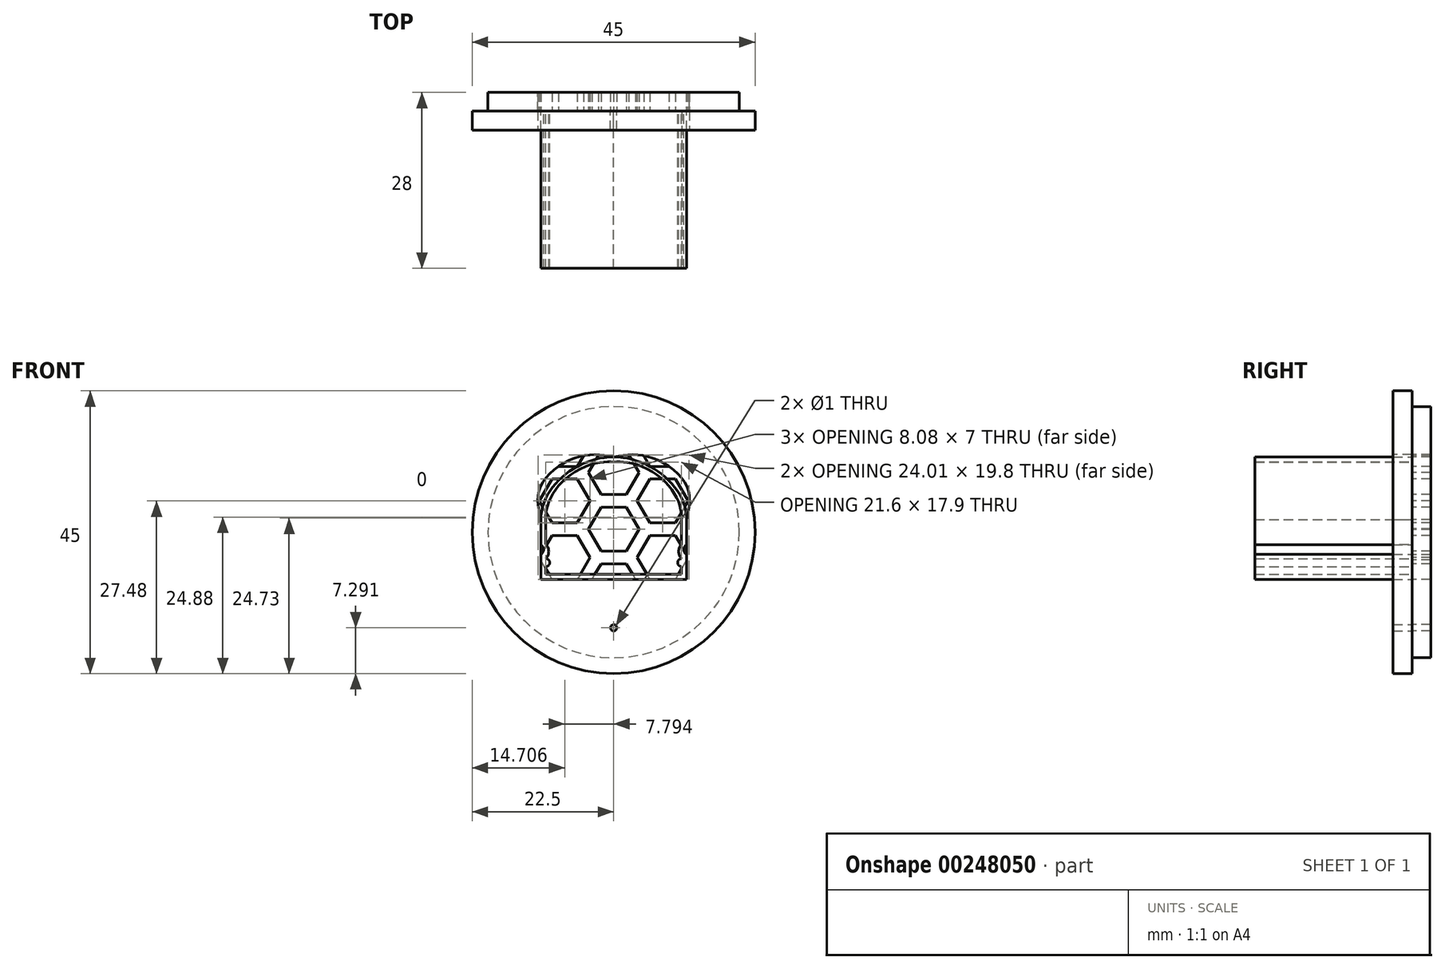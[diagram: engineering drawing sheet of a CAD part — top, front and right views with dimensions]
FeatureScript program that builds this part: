
annotation { "Feature Type Name" : "Feature", "Feature Type Description" : "" }
export const myFeature = defineFeature(function(context is Context, id is Id, definition is map)
    precondition{}
    {
        {
            var Q0;
            Q0=qCreatedBy(makeId("Front.planeOp"),FACE);
            var sketch = newSketch(context, id + "F0", { "sketchPlane" : qUnion([Q0])});
            skLineSegment(sketch, "E0", {"start": v(-11.6, 0) * mm, "end": v(11.6, 0) * mm});
            skLineSegment(sketch, "E1", {"start": v(11.6, 0) * mm, "end": v(11.6, 4) * mm});
            skLineSegment(sketch, "E2", {"start": v(11.6, 5.5) * mm, "end": v(11.6, 9.5) * mm});
            skLineSegment(sketch, "E3", {"start": v(0, 0) * mm, "end": v(0, 19.5) * mm, "construction": true});
            skFitSpline(sketch, "E4", {"points": [v(11.6, 9.5) * mm, v(0, 19.5) * mm], "startDerivative": vector(0, 16.22) * mm, "endDerivative": vector(-17.13, 0) * mm});
            skLineSegment(sketch, "E5", {"start": v(0, 0.8) * mm, "end": v(10.8, 0.8) * mm});
            skLineSegment(sketch, "E6", {"start": v(10.8, 0.8) * mm, "end": v(10.8, 2.05) * mm});
            skArc(sketch, "E7", {"start": v(10.8, 3.3) * mm, "mid": v(10.17, 2.67) * mm, "end": v(10.8, 2.05) * mm});
            skArc(sketch, "E8", {"start": v(10.8, 5.6) * mm, "mid": v(10.34, 4.45) * mm, "end": v(10.8, 3.3) * mm});
            skArc(sketch, "E9", {"start": v(11.6, 5.5) * mm, "mid": v(11.15, 4.75) * mm, "end": v(11.6, 4) * mm});
            skLineSegment(sketch, "E10.1", {"start": v(10.8, 5.6) * mm, "end": v(10.8, 9.5) * mm});
            skLineSegment(sketch, "E11.MirrorCS", {"start": v(-10.8, 0.8) * mm, "end": v(-10.8, 2.05) * mm});
            skArc(sketch, "E12.MirrorCS", {"start": v(-11.6, 5.5) * mm, "mid": v(-11.15, 4.75) * mm, "end": v(-11.6, 4) * mm});
            skLineSegment(sketch, "E13.MirrorCS", {"start": v(-11.6, 0) * mm, "end": v(-11.6, 4) * mm});
            skLineSegment(sketch, "E14.MirrorCS", {"start": v(-11.6, 5.5) * mm, "end": v(-11.6, 9.5) * mm});
            skFitSpline(sketch, "E15.MirrorCS", {"points": [v(-11.6, 9.5) * mm, v(0, 19.5) * mm], "startDerivative": vector(0, 16.22) * mm, "endDerivative": vector(17.13, 0) * mm});
            skLineSegment(sketch, "E16.MirrorCS", {"start": v(0, 0.8) * mm, "end": v(-10.8, 0.8) * mm});
            skArc(sketch, "E17.MirrorCS", {"start": v(-10.8, 5.6) * mm, "mid": v(-10.34, 4.45) * mm, "end": v(-10.8, 3.3) * mm});
            skArc(sketch, "E18.MirrorCS", {"start": v(-10.8, 3.3) * mm, "mid": v(-10.17, 2.67) * mm, "end": v(-10.8, 2.05) * mm});
            skLineSegment(sketch, "E19.MirrorCS", {"start": v(-10.8, 5.6) * mm, "end": v(-10.8, 9.5) * mm});
            skFitSpline(sketch, "E20.0", {"points": [v(-10.8, 9.5) * mm, v(-10.8, 10.1) * mm, v(-10.64, 11.29) * mm, v(-9.72, 13.55) * mm, v(-7.6, 16.07) * mm, v(-4.01, 18.17) * mm, v(-1.32, 18.7) * mm, v(0, 18.7) * mm]});
            skFitSpline(sketch, "E20.1", {"points": [v(10.8, 9.5) * mm, v(10.8, 10.1) * mm, v(10.64, 11.29) * mm, v(9.72, 13.55) * mm, v(7.6, 16.07) * mm, v(4.01, 18.17) * mm, v(1.32, 18.7) * mm, v(0, 18.7) * mm]});
            skSolve(sketch);
        }
        {
            var Q0;
            Q0=makeQuery(id+"F0.imprint","IMPRINT",FACE,{"disambiguationData":[TD([[makeQuery(id+"F0.imprint","IMPRINT",EDGE,{"derivedFrom":sQuery(id+"F0.wireOp",EDGE,"E0")}),1.0]])]});
            extrude(context, id + "F1", {"entities" : qUnion([Q0]), "depth" : 25 * mm});
        }
        {
            var Q0;
            Q0=qCreatedBy(makeId("Front.planeOp"),FACE);
            var sketch = newSketch(context, id + "F2", { "sketchPlane" : qUnion([Q0])});
            skFitSpline(sketch, "E21.0.0", {"points": [v(0, 19.5) * mm, v(-5.7, 19.5) * mm, v(-11.6, 14.9) * mm, v(-11.6, 9.5) * mm]});
            skLineSegment(sketch, "E21.0.1", {"start": v(-11.6, 9.5) * mm, "end": v(-11.6, 5.5) * mm});
            skLineSegment(sketch, "E21.0.3", {"start": v(-11.6, 4) * mm, "end": v(-11.6, 0) * mm});
            skLineSegment(sketch, "E21.0.4", {"start": v(-11.6, 0) * mm, "end": v(11.6, 0) * mm});
            skLineSegment(sketch, "E21.0.5", {"start": v(11.6, 0) * mm, "end": v(11.6, 4) * mm});
            skLineSegment(sketch, "E21.0.7", {"start": v(11.6, 5.5) * mm, "end": v(11.6, 9.5) * mm});
            skFitSpline(sketch, "E21.0.8", {"points": [v(11.6, 9.5) * mm, v(11.6, 14.9) * mm, v(5.7, 19.5) * mm, v(0, 19.5) * mm]});
            skLineSegment(sketch, "E22", {"start": v(-11.6, 5.5) * mm, "end": v(-11.6, 4) * mm});
            skLineSegment(sketch, "E23", {"start": v(11.6, 5.5) * mm, "end": v(11.6, 4) * mm});
            skCircle(sketch, "E24", {"center": v(0, 7.52) * mm, "radius": 20 * mm});
            skCircle(sketch, "E25", {"center": v(0, 7.52) * mm, "radius": 15.21 * mm, "construction": true});
            skCircle(sketch, "E26", {"center": v(0, 7.52) * mm, "radius": 22.5 * mm});
            skCircle(sketch, "E27", {"center": v(0, -7.69) * mm, "radius": 0.5 * mm});
            skSolve(sketch);
        }
        {
            var Q0;
            Q0=makeQuery(id+"F2.imprint","IMPRINT",FACE,{"disambiguationData":[TD([[makeQuery(id+"F2.imprint","IMPRINT",EDGE,{"derivedFrom":sQuery(id+"F2.wireOp",EDGE,"E24")}),-1.0]])]});
            var Q1;
            Q1=makeQuery(id+"F2.imprint","IMPRINT",FACE,{"disambiguationData":[TD([[makeQuery(id+"F2.imprint","IMPRINT",EDGE,{"derivedFrom":sQuery(id+"F2.wireOp",EDGE,"806d5c89-55b4-439b-8d5d-3d22e5748bae.0")}),1.0]])]});
            var Q2;
            Q2=makeQuery(id+"F2.imprint","IMPRINT",FACE,{"disambiguationData":[TD([[makeQuery(id+"F2.imprint","IMPRINT",EDGE,{"derivedFrom":sQuery(id+"F2.wireOp",EDGE,"E21.0.0")}),-1.0]])]});
            extrude(context, id + "F3", {"entities" : qUnion([Q0, Q1, Q2]), "depth" : 3 * mm});
        }
        {
            var Q0;
            Q0=qCreatedBy(makeId("Front.planeOp"),FACE);
            var sketch = newSketch(context, id + "F4", { "sketchPlane" : qUnion([Q0])});
            skCircle(sketch, "E28.cCircle", {"center": v(-15.59, -1) * mm, "radius": 3.5 * mm, "construction": true});
            skLineSegment(sketch, "E28.0", {"start": v(-17.6, 2.5) * mm, "end": v(-13.57, 2.5) * mm});
            skLineSegment(sketch, "E28.1", {"start": v(-13.57, 2.5) * mm, "end": v(-11.55, -1) * mm});
            skLineSegment(sketch, "E28.2", {"start": v(-11.55, -1) * mm, "end": v(-13.57, -4.5) * mm});
            skLineSegment(sketch, "E28.3", {"start": v(-13.57, -4.5) * mm, "end": v(-17.6, -4.5) * mm});
            skLineSegment(sketch, "E28.4", {"start": v(-17.6, -4.5) * mm, "end": v(-19.63, -1) * mm});
            skLineSegment(sketch, "E28.5", {"start": v(-19.63, -1) * mm, "end": v(-17.6, 2.5) * mm});
            skPoint(sketch, "E28.0.midPoint", {"position": v(-15.59, 2.5) * mm});
            skCircle(sketch, "E29.cCircle", {"center": v(-7.8, -5.5) * mm, "radius": 3.5 * mm, "construction": true});
            skLineSegment(sketch, "E29.0", {"start": v(-9.81, -2) * mm, "end": v(-5.77, -2) * mm});
            skLineSegment(sketch, "E29.1", {"start": v(-5.77, -2) * mm, "end": v(-3.75, -5.5) * mm});
            skLineSegment(sketch, "E29.2", {"start": v(-3.75, -5.5) * mm, "end": v(-5.77, -9) * mm});
            skLineSegment(sketch, "E29.3", {"start": v(-5.77, -9) * mm, "end": v(-9.81, -9) * mm});
            skLineSegment(sketch, "E29.4", {"start": v(-9.81, -9) * mm, "end": v(-11.84, -5.5) * mm});
            skLineSegment(sketch, "E29.5", {"start": v(-11.84, -5.5) * mm, "end": v(-9.81, -2) * mm});
            skPoint(sketch, "E29.0.midPoint", {"position": v(-7.8, -2) * mm});
            skLineSegment(sketch, "E30", {"start": v(-15.59, -1) * mm, "end": v(-7.8, -5.5) * mm, "construction": true});
            skLineSegment(sketch, "E31", {"start": v(-11.84, -5.5) * mm, "end": v(-13.57, -4.5) * mm, "construction": true});
            skLineSegment(sketch, "E32.0.1.0", {"start": v(-21.36, 16) * mm, "end": v(-19.34, 12.5) * mm});
            skLineSegment(sketch, "E32.0.1.1", {"start": v(-25.4, 16) * mm, "end": v(-21.36, 16) * mm});
            skLineSegment(sketch, "E32.0.1.2", {"start": v(-27.42, 12.5) * mm, "end": v(-25.4, 16) * mm});
            skLineSegment(sketch, "E32.0.1.3", {"start": v(-25.4, 9) * mm, "end": v(-27.42, 12.5) * mm});
            skLineSegment(sketch, "E32.0.1.4", {"start": v(-21.36, 9) * mm, "end": v(-25.4, 9) * mm});
            skLineSegment(sketch, "E32.0.1.5", {"start": v(-19.34, 12.5) * mm, "end": v(-21.36, 9) * mm});
            skLineSegment(sketch, "E32.0.1.6", {"start": v(-19.63, 8) * mm, "end": v(-17.6, 11.5) * mm});
            skLineSegment(sketch, "E32.0.1.7", {"start": v(-17.6, 4.5) * mm, "end": v(-19.63, 8) * mm});
            skLineSegment(sketch, "E32.0.1.8", {"start": v(-13.57, 4.5) * mm, "end": v(-17.6, 4.5) * mm});
            skLineSegment(sketch, "E32.0.1.9", {"start": v(-11.55, 8) * mm, "end": v(-13.57, 4.5) * mm});
            skLineSegment(sketch, "E32.0.1.10", {"start": v(-13.57, 11.5) * mm, "end": v(-11.55, 8) * mm});
            skLineSegment(sketch, "E32.0.1.11", {"start": v(-17.6, 11.5) * mm, "end": v(-13.57, 11.5) * mm});
            skLineSegment(sketch, "E32.1.0.0", {"start": v(-5.77, 7) * mm, "end": v(-3.75, 3.5) * mm});
            skLineSegment(sketch, "E32.1.0.1", {"start": v(-9.81, 7) * mm, "end": v(-5.77, 7) * mm});
            skLineSegment(sketch, "E32.1.0.2", {"start": v(-11.84, 3.5) * mm, "end": v(-9.81, 7) * mm});
            skLineSegment(sketch, "E32.1.0.3", {"start": v(-9.81, 0) * mm, "end": v(-11.84, 3.5) * mm});
            skLineSegment(sketch, "E32.1.0.4", {"start": v(-5.77, 0) * mm, "end": v(-9.81, 0) * mm});
            skLineSegment(sketch, "E32.1.0.5", {"start": v(-3.75, 3.5) * mm, "end": v(-5.77, 0) * mm});
            skLineSegment(sketch, "E32.1.0.6", {"start": v(-4.04, -1) * mm, "end": v(-2.02, 2.5) * mm});
            skLineSegment(sketch, "E32.1.0.7", {"start": v(-2.02, -4.5) * mm, "end": v(-4.04, -1) * mm});
            skLineSegment(sketch, "E32.1.0.8", {"start": v(2.02, -4.5) * mm, "end": v(-2.02, -4.5) * mm});
            skLineSegment(sketch, "E32.1.0.9", {"start": v(4.04, -1) * mm, "end": v(2.02, -4.5) * mm});
            skLineSegment(sketch, "E32.1.0.10", {"start": v(2.02, 2.5) * mm, "end": v(4.04, -1) * mm});
            skLineSegment(sketch, "E32.1.0.11", {"start": v(-2.02, 2.5) * mm, "end": v(2.02, 2.5) * mm});
            skLineSegment(sketch, "E32.1.1.0", {"start": v(-13.57, 20.5) * mm, "end": v(-11.55, 17) * mm});
            skLineSegment(sketch, "E32.1.1.1", {"start": v(-17.6, 20.5) * mm, "end": v(-13.57, 20.5) * mm});
            skLineSegment(sketch, "E32.1.1.2", {"start": v(-19.63, 17) * mm, "end": v(-17.6, 20.5) * mm});
            skLineSegment(sketch, "E32.1.1.3", {"start": v(-17.6, 13.5) * mm, "end": v(-19.63, 17) * mm});
            skLineSegment(sketch, "E32.1.1.4", {"start": v(-13.57, 13.5) * mm, "end": v(-17.6, 13.5) * mm});
            skLineSegment(sketch, "E32.1.1.5", {"start": v(-11.55, 17) * mm, "end": v(-13.57, 13.5) * mm});
            skLineSegment(sketch, "E32.1.1.6", {"start": v(-11.84, 12.5) * mm, "end": v(-9.81, 16) * mm});
            skLineSegment(sketch, "E32.1.1.7", {"start": v(-9.81, 9) * mm, "end": v(-11.84, 12.5) * mm});
            skLineSegment(sketch, "E32.1.1.8", {"start": v(-5.77, 9) * mm, "end": v(-9.81, 9) * mm});
            skLineSegment(sketch, "E32.1.1.9", {"start": v(-3.75, 12.5) * mm, "end": v(-5.77, 9) * mm});
            skLineSegment(sketch, "E32.1.1.10", {"start": v(-5.77, 16) * mm, "end": v(-3.75, 12.5) * mm});
            skLineSegment(sketch, "E32.1.1.11", {"start": v(-9.81, 16) * mm, "end": v(-5.77, 16) * mm});
            skLineSegment(sketch, "E32.2.0.0", {"start": v(2.02, 11.5) * mm, "end": v(4.04, 8) * mm});
            skLineSegment(sketch, "E32.2.0.1", {"start": v(-2.02, 11.5) * mm, "end": v(2.02, 11.5) * mm});
            skLineSegment(sketch, "E32.2.0.2", {"start": v(-4.04, 8) * mm, "end": v(-2.02, 11.5) * mm});
            skLineSegment(sketch, "E32.2.0.3", {"start": v(-2.02, 4.5) * mm, "end": v(-4.04, 8) * mm});
            skLineSegment(sketch, "E32.2.0.4", {"start": v(2.02, 4.5) * mm, "end": v(-2.02, 4.5) * mm});
            skLineSegment(sketch, "E32.2.0.5", {"start": v(4.04, 8) * mm, "end": v(2.02, 4.5) * mm});
            skLineSegment(sketch, "E32.2.0.6", {"start": v(3.75, 3.5) * mm, "end": v(5.77, 7) * mm});
            skLineSegment(sketch, "E32.2.0.7", {"start": v(5.77, 0) * mm, "end": v(3.75, 3.5) * mm});
            skLineSegment(sketch, "E32.2.0.8", {"start": v(9.81, 0) * mm, "end": v(5.77, 0) * mm});
            skLineSegment(sketch, "E32.2.0.9", {"start": v(11.84, 3.5) * mm, "end": v(9.81, 0) * mm});
            skLineSegment(sketch, "E32.2.0.10", {"start": v(9.81, 7) * mm, "end": v(11.84, 3.5) * mm});
            skLineSegment(sketch, "E32.2.0.11", {"start": v(5.77, 7) * mm, "end": v(9.81, 7) * mm});
            skLineSegment(sketch, "E32.2.1.0", {"start": v(-5.77, 25) * mm, "end": v(-3.75, 21.5) * mm});
            skLineSegment(sketch, "E32.2.1.1", {"start": v(-9.81, 25) * mm, "end": v(-5.77, 25) * mm});
            skLineSegment(sketch, "E32.2.1.2", {"start": v(-11.84, 21.5) * mm, "end": v(-9.81, 25) * mm});
            skLineSegment(sketch, "E32.2.1.3", {"start": v(-9.81, 18) * mm, "end": v(-11.84, 21.5) * mm});
            skLineSegment(sketch, "E32.2.1.4", {"start": v(-5.77, 18) * mm, "end": v(-9.81, 18) * mm});
            skLineSegment(sketch, "E32.2.1.5", {"start": v(-3.75, 21.5) * mm, "end": v(-5.77, 18) * mm});
            skLineSegment(sketch, "E32.2.1.6", {"start": v(-4.04, 17) * mm, "end": v(-2.02, 20.5) * mm});
            skLineSegment(sketch, "E32.2.1.7", {"start": v(-2.02, 13.5) * mm, "end": v(-4.04, 17) * mm});
            skLineSegment(sketch, "E32.2.1.8", {"start": v(2.02, 13.5) * mm, "end": v(-2.02, 13.5) * mm});
            skLineSegment(sketch, "E32.2.1.9", {"start": v(4.04, 17) * mm, "end": v(2.02, 13.5) * mm});
            skLineSegment(sketch, "E32.2.1.10", {"start": v(2.02, 20.5) * mm, "end": v(4.04, 17) * mm});
            skLineSegment(sketch, "E32.2.1.11", {"start": v(-2.02, 20.5) * mm, "end": v(2.02, 20.5) * mm});
            skLineSegment(sketch, "E32.direction1", {"start": v(-11.55, -1) * mm, "end": v(-3.75, 3.5) * mm, "construction": true});
            skLineSegment(sketch, "E32.direction2", {"start": v(-11.55, -1) * mm, "end": v(-19.34, 12.5) * mm, "construction": true});
            skLineSegment(sketch, "E33", {"start": v(-5.77, 7) * mm, "end": v(-5.77, 9) * mm, "construction": true});
            skLineSegment(sketch, "E34.0.3.0", {"start": v(9.81, 16) * mm, "end": v(11.84, 12.5) * mm});
            skLineSegment(sketch, "E34.3.3.0", {"start": v(5.77, 16) * mm, "end": v(9.81, 16) * mm});
            skLineSegment(sketch, "E34.6.3.0", {"start": v(3.75, 12.5) * mm, "end": v(5.77, 16) * mm});
            skLineSegment(sketch, "E34.9.3.0", {"start": v(5.77, 9) * mm, "end": v(3.75, 12.5) * mm});
            skLineSegment(sketch, "E34.12.3.0", {"start": v(9.81, 9) * mm, "end": v(5.77, 9) * mm});
            skLineSegment(sketch, "E34.15.3.0", {"start": v(11.84, 12.5) * mm, "end": v(9.81, 9) * mm});
            skLineSegment(sketch, "E34.18.3.0", {"start": v(11.55, 8) * mm, "end": v(13.57, 11.5) * mm});
            skLineSegment(sketch, "E34.21.3.0", {"start": v(13.57, 4.5) * mm, "end": v(11.55, 8) * mm});
            skLineSegment(sketch, "E34.24.3.0", {"start": v(17.6, 4.5) * mm, "end": v(13.57, 4.5) * mm});
            skLineSegment(sketch, "E34.27.3.0", {"start": v(19.63, 8) * mm, "end": v(17.6, 4.5) * mm});
            skLineSegment(sketch, "E34.30.3.0", {"start": v(17.6, 11.5) * mm, "end": v(19.63, 8) * mm});
            skLineSegment(sketch, "E34.33.3.0", {"start": v(13.57, 11.5) * mm, "end": v(17.6, 11.5) * mm});
            skLineSegment(sketch, "E34.0.3.1", {"start": v(2.02, 29.5) * mm, "end": v(4.04, 26) * mm});
            skLineSegment(sketch, "E34.3.3.1", {"start": v(-2.02, 29.5) * mm, "end": v(2.02, 29.5) * mm});
            skLineSegment(sketch, "E34.6.3.1", {"start": v(-4.04, 26) * mm, "end": v(-2.02, 29.5) * mm});
            skLineSegment(sketch, "E34.9.3.1", {"start": v(-2.02, 22.5) * mm, "end": v(-4.04, 26) * mm});
            skLineSegment(sketch, "E34.12.3.1", {"start": v(2.02, 22.5) * mm, "end": v(-2.02, 22.5) * mm});
            skLineSegment(sketch, "E34.15.3.1", {"start": v(4.04, 26) * mm, "end": v(2.02, 22.5) * mm});
            skLineSegment(sketch, "E34.18.3.1", {"start": v(3.75, 21.5) * mm, "end": v(5.77, 25) * mm});
            skLineSegment(sketch, "E34.21.3.1", {"start": v(5.77, 18) * mm, "end": v(3.75, 21.5) * mm});
            skLineSegment(sketch, "E34.24.3.1", {"start": v(9.81, 18) * mm, "end": v(5.77, 18) * mm});
            skLineSegment(sketch, "E34.27.3.1", {"start": v(11.84, 21.5) * mm, "end": v(9.81, 18) * mm});
            skLineSegment(sketch, "E34.30.3.1", {"start": v(9.81, 25) * mm, "end": v(11.84, 21.5) * mm});
            skLineSegment(sketch, "E34.33.3.1", {"start": v(5.77, 25) * mm, "end": v(9.81, 25) * mm});
            skPoint(sketch, "E35", {"position": v(0, 11.5) * mm});
            skLineSegment(sketch, "E36.0", {"start": v(-11.6, 0) * mm, "end": v(11.6, 0) * mm});
            skLineSegment(sketch, "E36.1", {"start": v(11.6, 0) * mm, "end": v(11.6, 9.5) * mm});
            skFitSpline(sketch, "E36.2", {"points": [v(11.6, 9.5) * mm, v(11.6, 14.9) * mm, v(5.7, 19.5) * mm, v(0, 19.5) * mm]});
            skFitSpline(sketch, "E36.3", {"points": [v(0, 19.5) * mm, v(-5.7, 19.5) * mm, v(-11.6, 14.9) * mm, v(-11.6, 9.5) * mm]});
            skLineSegment(sketch, "E36.4", {"start": v(-11.6, 9.5) * mm, "end": v(-11.6, 0) * mm});
            skSolve(sketch);
        }
        {
            var Q0;
            {var subQ12=sQuery(id+"F4.wireOp",EDGE,"E32.1.0.0");Q0=makeQuery(id+"F4.imprint","IMPRINT",FACE,{"disambiguationData":[TD([[makeQuery(id+"F4.imprint","IMPRINT",EDGE,{"derivedFrom":subQ12}),1.0]])]});}
            var Q1;
            {var subQ0=sQuery(id+"F4.wireOp",EDGE,"E36.0");var subQ1=sQuery(id+"F4.wireOp",EDGE,"E32.2.0.9");var subQ2=makeQuery(id+"F4.imprint","INTERSECT",VERTEX,{"derivedFrom":[subQ1,subQ0]});Q1=makeQuery(id+"F4.imprint","IMPRINT",FACE,{"disambiguationData":[TD([[makeQuery(id+"F4.imprint","IMPRINT",EDGE,{"disambiguationData":[TD([[subQ2,1.0]])],"derivedFrom":subQ1}),1.0]])]});}
            var Q2;
            {var subQ0=sQuery(id+"F4.wireOp",EDGE,"E36.0");var subQ1=sQuery(id+"F4.wireOp",EDGE,"E32.1.0.3");var subQ2=makeQuery(id+"F4.imprint","INTERSECT",VERTEX,{"derivedFrom":[subQ1,subQ0]});Q2=makeQuery(id+"F4.imprint","IMPRINT",FACE,{"disambiguationData":[TD([[makeQuery(id+"F4.imprint","IMPRINT",EDGE,{"disambiguationData":[TD([[subQ2,-1.0]])],"derivedFrom":subQ1}),1.0]])]});}
            var Q3;
            Q3=makeQuery(id+"F2.imprint","IMPRINT",FACE,{"disambiguationData":[TD([[makeQuery(id+"F2.imprint","IMPRINT",EDGE,{"derivedFrom":sQuery(id+"F2.wireOp",EDGE,"E21.0.0")}),-1.0]])]});
            extrude(context, id + "F5", {"entities" : qUnion([Q0, Q1, Q2, Q3]), "oppositeDirection" : true, "depth" : 3 * mm});
        }
    });
